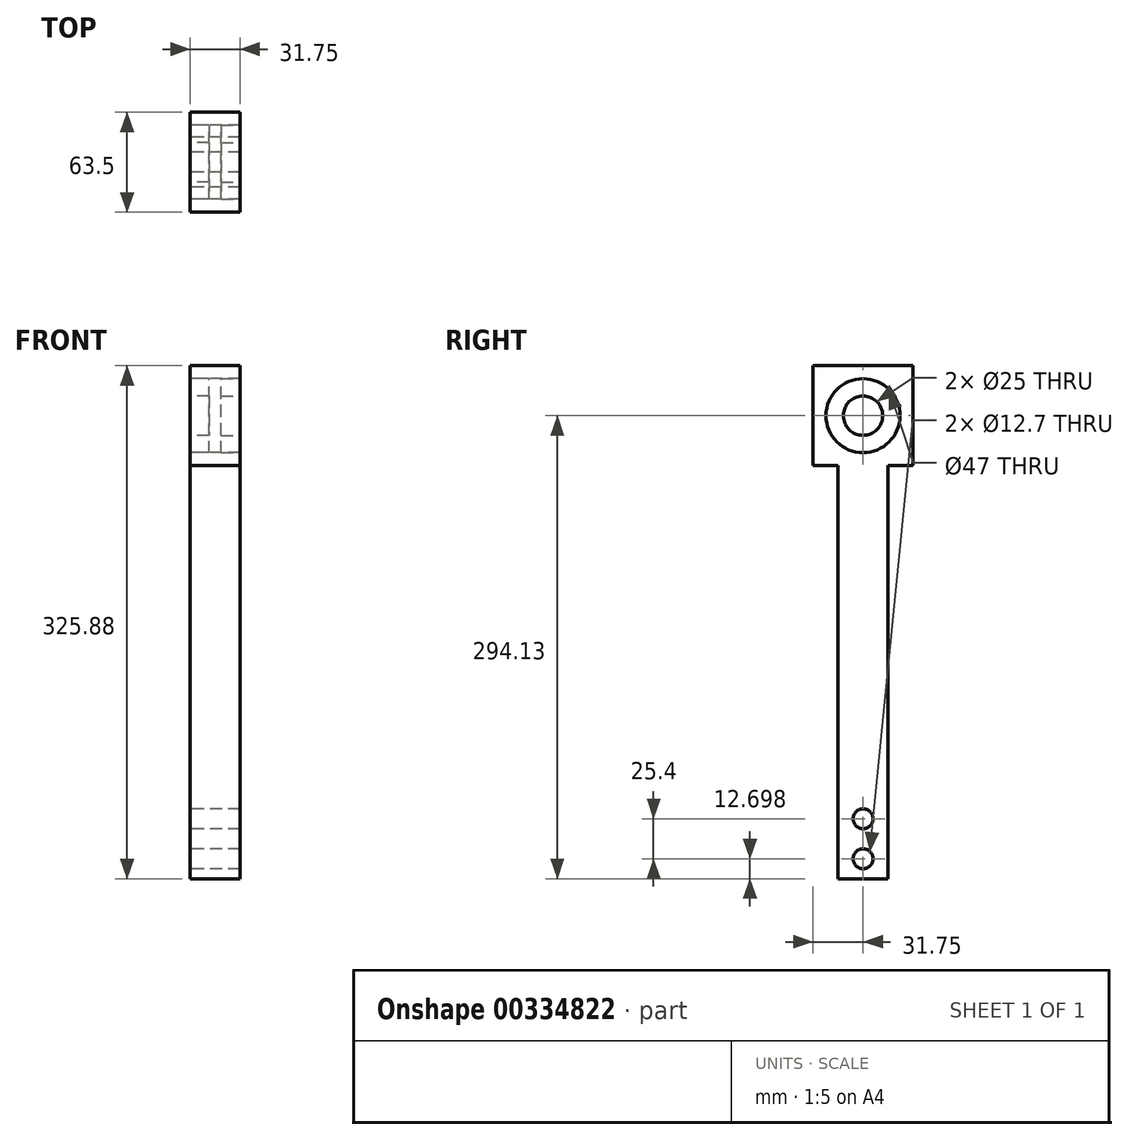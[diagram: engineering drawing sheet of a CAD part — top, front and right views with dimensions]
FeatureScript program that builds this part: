
annotation { "Feature Type Name" : "Feature", "Feature Type Description" : "" }
export const myFeature = defineFeature(function(context is Context, id is Id, definition is map)
    precondition{}
    {
        {
            var Q0;
            Q0=qCreatedBy(makeId("Right.planeOp"),FACE);
            var sketch = newSketch(context, id + "F0", { "sketchPlane" : qUnion([Q0])});
            skLineSegment(sketch, "E0.bottom", {"start": v(31.75, -31.75) * mm, "end": v(15.87, -31.75) * mm});
            skLineSegment(sketch, "E0.top", {"start": v(31.75, 31.75) * mm, "end": v(-31.75, 31.75) * mm});
            skLineSegment(sketch, "E0.left", {"start": v(31.75, -31.75) * mm, "end": v(31.75, 31.75) * mm});
            skLineSegment(sketch, "E0.right", {"start": v(-31.75, -31.75) * mm, "end": v(-31.75, 31.75) * mm});
            skPoint(sketch, "E0.middle", {"position": v(0, 0) * mm});
            skLineSegment(sketch, "E1.top", {"start": v(-15.88, -294.13) * mm, "end": v(15.88, -294.13) * mm});
            skLineSegment(sketch, "E1.left", {"start": v(-15.88, -31.75) * mm, "end": v(-15.88, -294.13) * mm});
            skLineSegment(sketch, "E1.right", {"start": v(15.87, -31.75) * mm, "end": v(15.87, -294.13) * mm});
            skLineSegment(sketch, "E2", {"start": v(0, 0) * mm, "end": v(0, -24.97) * mm, "construction": true});
            skPoint(sketch, "E2.endSnap0", {"position": v(0, -31.75) * mm});
            skCircle(sketch, "E3", {"center": v(0, 0) * mm, "radius": 23.5 * mm});
            skLineSegment(sketch, "E4.trimOffspring", {"start": v(-15.88, -31.75) * mm, "end": v(-31.75, -31.75) * mm});
            skLineSegment(sketch, "E5", {"start": v(0, -31.75) * mm, "end": v(0, -294.13) * mm, "construction": true});
            skCircle(sketch, "E6", {"center": v(0, -256.03) * mm, "radius": 6.35 * mm});
            skCircle(sketch, "E7", {"center": v(0, -281.43) * mm, "radius": 6.35 * mm});
            skSolve(sketch);
        }
        {
            var Q0;
            Q0 = qSketchRegion(id + "F0", true);
            extrude(context, id + "F1", {"entities" : qUnion([Q0]), "depth" : 31.75 * mm});
        }
        {
            var Q0;
            Q0=makeQuery(id+"F1.opExtrude","CAP_FACE",FACE,{"disambiguationData":[OSD([sQuery(id+"F0.wireOp",EDGE,"E0.bottom"),sQuery(id+"F0.wireOp",EDGE,"E0.top"),sQuery(id+"F0.wireOp",EDGE,"E0.left"),sQuery(id+"F0.wireOp",EDGE,"E0.right"),sQuery(id+"F0.wireOp",EDGE,"E1.top"),sQuery(id+"F0.wireOp",EDGE,"E1.left"),sQuery(id+"F0.wireOp",EDGE,"E1.right"),sQuery(id+"F0.wireOp",EDGE,"E3"),sQuery(id+"F0.wireOp",EDGE,"E4.trimOffspring"),sQuery(id+"F0.wireOp",EDGE,"E6"),sQuery(id+"F0.wireOp",EDGE,"E7")])],"isStart":false});
            var sketch = newSketch(context, id + "F2", { "sketchPlane" : qUnion([Q0])});
            skCircle(sketch, "E8.0", {"center": v(0, 0) * mm, "radius": 23.5 * mm});
            skCircle(sketch, "E9", {"center": v(0, 0) * mm, "radius": 12.5 * mm});
            skSolve(sketch);
        }
        {
            var Q0;
            Q0 = qSketchRegion(id + "F2", true);
            extrude(context, id + "F3", {"entities" : qUnion([Q0]), "oppositeDirection" : true, "depth" : 12 * mm});
        }
        {
            var Q0;
            Q0=makeQuery(id+"F1.opExtrude","CAP_FACE",FACE,{"disambiguationData":[OSD([sQuery(id+"F0.wireOp",EDGE,"E0.bottom"),sQuery(id+"F0.wireOp",EDGE,"E0.top"),sQuery(id+"F0.wireOp",EDGE,"E0.left"),sQuery(id+"F0.wireOp",EDGE,"E0.right"),sQuery(id+"F0.wireOp",EDGE,"E1.top"),sQuery(id+"F0.wireOp",EDGE,"E1.left"),sQuery(id+"F0.wireOp",EDGE,"E1.right"),sQuery(id+"F0.wireOp",EDGE,"E3"),sQuery(id+"F0.wireOp",EDGE,"E4.trimOffspring"),sQuery(id+"F0.wireOp",EDGE,"E6"),sQuery(id+"F0.wireOp",EDGE,"E7")])],"isStart":true});
            var sketch = newSketch(context, id + "F4", { "sketchPlane" : qUnion([Q0])});
            skCircle(sketch, "E10.0", {"center": v(0, 0) * mm, "radius": 23.5 * mm});
            skCircle(sketch, "E11.0", {"center": v(0, 0) * mm, "radius": 12.5 * mm});
            skSolve(sketch);
        }
        {
            var Q0;
            Q0 = qSketchRegion(id + "F4", true);
            extrude(context, id + "F5", {"entities" : qUnion([Q0]), "oppositeDirection" : true, "depth" : 12 * mm});
        }
    });
